# Revit family: Genelec_4020
name_source: partatom
category: Generic Models
units: mm (PartAtom-declared; Revit-internal decimal feet)

## family parameters
Always vertical = No
Can host rebar = No
Cut with Voids When Loaded = No
Maintain Annotation Orientation = No
Part Type = Normal
Room Calculation Point = Yes
Round Connector Dimension = Use Diameter
Shared = No
Work Plane-Based = No

## types (2) — shared parameters
Accuracy of Frequency Response = ± 2.5 dB (62 Hz - 20 kHz)
Acoustic Axis = 130
BIMobject category = Audio Electronics
Color = RAL_9018_Papyrus White
Connections = 1 x Euroblock Analog Input
1 x Euroblock Analog Input
1 x Euroblock Analog Input
1 x Euroblock Analog Input
Default Elevation = 1200 mm
Depth = 142 mm  [stored 0.465879 ft]
Description = The 4020C Active Installation Loudspeaker offers huge performance in a compact aluminium cabinet with tightly controlled directivity and minimum diffraction for excellent performance.
Dispersion Angle = H 120° V 100°
Driver Dimensions = ⌀ 105 mm Woofer + ⌀ 19 mm Tweeter
Export Type to IFC As = IfcAudioVisualApplianceType
Finish Type = Die cast aluminium
Frequency Response = 56 Hz - 25 kHz (-6 dB)
Height = 226 mm  [stored 0.74147 ft]
IFC Classification = Electric Appliance
IFC Name = 4020C
Line Drawing = https://assets.ctfassets.net
Mains Voltage = 100-240 VAC 50/60Hz
Manufacturer = GENELEC
Manufacturer Country = Finland
Max. short term sine wave acoustic output  on axis in half space, averaged from 100Hz to 3 kHz = ≥100 dB
Maximum long term RMS acoustic output in same conditions with IEC weighted noise (limited by driver unit protection circuit) = ≥93 dB
Model = 4020C
Model Description = Active Installation Speaker
Model Image = https://images.ctfassets.net
Model Name = 4020C
Mounting Type = Includes mount: 4000-410B/W
Power Consumption = 60 W
Power consumption Idle = ≤3 W
Power consumption Standby = ≤0.5 W (ISS Active)
Price List Description = Compact aluminium cabinet with tightly controlled directivity and minimum diffraction for excellent performance. Both drivers have metal protection grilles, with 76 mm (3 in) LF and 19 mm (3/4 in)  HF transducers.  Integrated crossover and Class D amplifiers 25 W + 25 W. Max. SPL 96 dB, frequency response 67 Hz - 25 kHz (- 6 dB). 

Room response controls on rear panel to compensate the placement and room effects. On-Off switch on the rear panel. Dimensions: H 181 x W 121 x D 115 mm, weight 1,5 kg.
Product Family = Installation Speaker
Product Group = 4000 Series Installation Speakers
Self-generated Noise = ≤5 dB
Type IFC Predefined Type = SPEAKER
Type Image = <None>
URL = https://www.genelec.com
Uniclass 2.0 Description = Sound Amplifiers
Weight = 3.1
Width = 151 mm  [stored 0.495407 ft]

## per-type parameters (varying)
| type | Horizontal Visibility | Vertical Visibility |
| 4020 Vertical | No | Yes |
| 4020 Horizontal | Yes | No |

note: [stored X ft] marks values corroborated as IEEE doubles in the binary element streams (Revit-internal decimal feet)

## geometry (parser evidence)
native form markers: Sweep x2
no freeform markers — native parametric forms only
